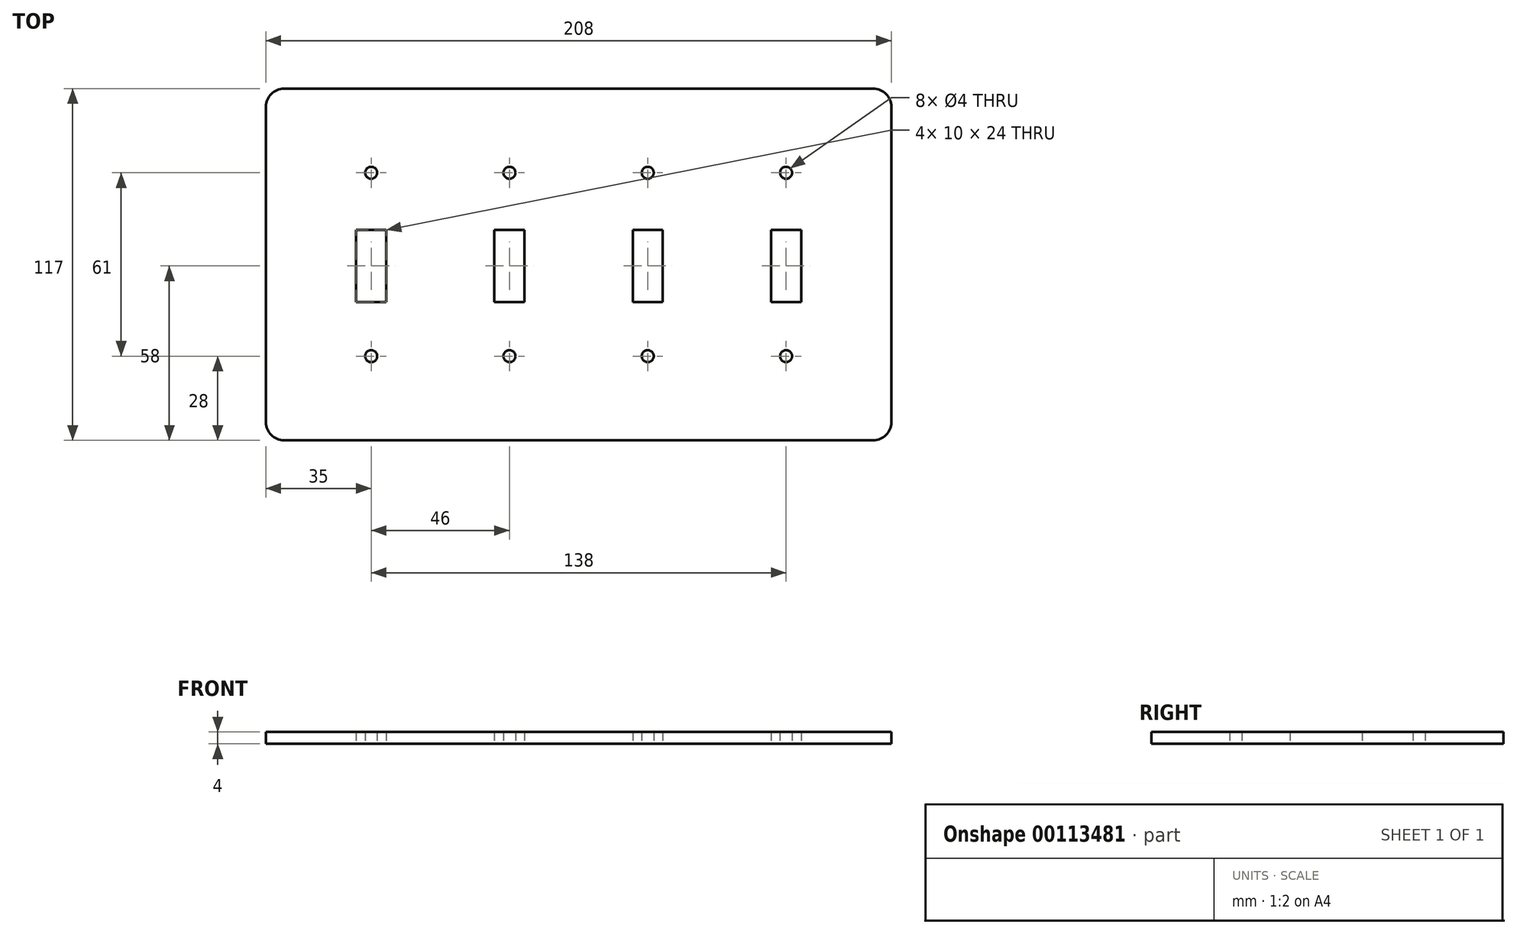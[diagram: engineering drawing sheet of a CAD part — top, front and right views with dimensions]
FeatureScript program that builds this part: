
annotation { "Feature Type Name" : "Feature", "Feature Type Description" : "" }
export const myFeature = defineFeature(function(context is Context, id is Id, definition is map)
    precondition{}
    {
        {
            var Q0;
            Q0=qCreatedBy(makeId("Top.planeOp"),FACE);
            var sketch = newSketch(context, id + "F0", { "sketchPlane" : qUnion([Q0])});
            skLineSegment(sketch, "E0.bottom", {"start": v(0, 0) * mm, "end": v(208, 0) * mm});
            skLineSegment(sketch, "E0.top", {"start": v(0, 117) * mm, "end": v(208, 117) * mm});
            skLineSegment(sketch, "E0.left", {"start": v(0, 0) * mm, "end": v(0, 117) * mm});
            skLineSegment(sketch, "E0.right", {"start": v(208, 0) * mm, "end": v(208, 117) * mm});
            skLineSegment(sketch, "E1.bottom", {"start": v(168, 70) * mm, "end": v(178, 70) * mm});
            skLineSegment(sketch, "E1.top", {"start": v(168, 46) * mm, "end": v(178, 46) * mm});
            skLineSegment(sketch, "E1.left", {"start": v(168, 70) * mm, "end": v(168, 46) * mm});
            skLineSegment(sketch, "E1.right", {"start": v(178, 70) * mm, "end": v(178, 46) * mm});
            skCircle(sketch, "E2", {"center": v(173, 89) * mm, "radius": 2 * mm});
            skCircle(sketch, "E3", {"center": v(173, 28) * mm, "radius": 2 * mm});
            skLineSegment(sketch, "E4.1.0.0", {"start": v(122, 70) * mm, "end": v(122, 46) * mm});
            skLineSegment(sketch, "E4.1.0.1", {"start": v(122, 46) * mm, "end": v(132, 46) * mm});
            skLineSegment(sketch, "E4.1.0.2", {"start": v(122, 70) * mm, "end": v(132, 70) * mm});
            skLineSegment(sketch, "E4.1.0.3", {"start": v(132, 70) * mm, "end": v(132, 46) * mm});
            skCircle(sketch, "E4.1.0.4", {"center": v(127, 89) * mm, "radius": 2 * mm});
            skCircle(sketch, "E4.1.0.5", {"center": v(127, 28) * mm, "radius": 2 * mm});
            skLineSegment(sketch, "E4.2.0.0", {"start": v(76, 70) * mm, "end": v(76, 46) * mm});
            skLineSegment(sketch, "E4.2.0.1", {"start": v(76, 46) * mm, "end": v(86, 46) * mm});
            skLineSegment(sketch, "E4.2.0.2", {"start": v(76, 70) * mm, "end": v(86, 70) * mm});
            skLineSegment(sketch, "E4.2.0.3", {"start": v(86, 70) * mm, "end": v(86, 46) * mm});
            skCircle(sketch, "E4.2.0.4", {"center": v(81, 89) * mm, "radius": 2 * mm});
            skCircle(sketch, "E4.2.0.5", {"center": v(81, 28) * mm, "radius": 2 * mm});
            skLineSegment(sketch, "E4.direction1", {"start": v(173, 28) * mm, "end": v(127, 28) * mm, "construction": true});
            skLineSegment(sketch, "E5.0.3.0", {"start": v(30, 70) * mm, "end": v(30, 46) * mm});
            skLineSegment(sketch, "E5.3.3.0", {"start": v(30, 46) * mm, "end": v(40, 46) * mm});
            skLineSegment(sketch, "E5.6.3.0", {"start": v(30, 70) * mm, "end": v(40, 70) * mm});
            skLineSegment(sketch, "E5.9.3.0", {"start": v(40, 70) * mm, "end": v(40, 46) * mm});
            skCircle(sketch, "E5.12.3.0", {"center": v(35, 89) * mm, "radius": 2 * mm});
            skCircle(sketch, "E5.14.3.0", {"center": v(35, 28) * mm, "radius": 2 * mm});
            skSolve(sketch);
        }
        {
            var Q0;
            Q0=qSketchRegion(id+"F0",true);
            extrude(context, id + "F1", {"entities" : qUnion([Q0]), "depth" : 4 * mm});
        }
        {
            var Q0;
            Q0=makeQuery(id+"F1.opExtrude","SWEPT_EDGE",EDGE,{"disambiguationData":[OSD([sQuery(id+"F0.wireOp",EDGE,"E0.top"),sQuery(id+"F0.wireOp",EDGE,"E0.left")])]});
            var Q1;
            Q1=makeQuery(id+"F1.opExtrude","SWEPT_EDGE",EDGE,{"disambiguationData":[OSD([sQuery(id+"F0.wireOp",EDGE,"E0.top"),sQuery(id+"F0.wireOp",EDGE,"E0.right")])]});
            var Q2;
            Q2=makeQuery(id+"F1.opExtrude","SWEPT_EDGE",EDGE,{"disambiguationData":[OSD([sQuery(id+"F0.wireOp",EDGE,"E0.bottom"),sQuery(id+"F0.wireOp",EDGE,"E0.right")])]});
            var Q3;
            Q3=makeQuery(id+"F1.opExtrude","SWEPT_EDGE",EDGE,{"disambiguationData":[OSD([sQuery(id+"F0.wireOp",EDGE,"E0.bottom"),sQuery(id+"F0.wireOp",EDGE,"E0.left")])]});
            fillet(context, id + "F2", {"entities" : qUnion([Q0, Q1, Q2, Q3]), "radius" : 6 * mm, "tangentPropagation" : true, "allowEdgeOverflow" : false});
        }
    });
